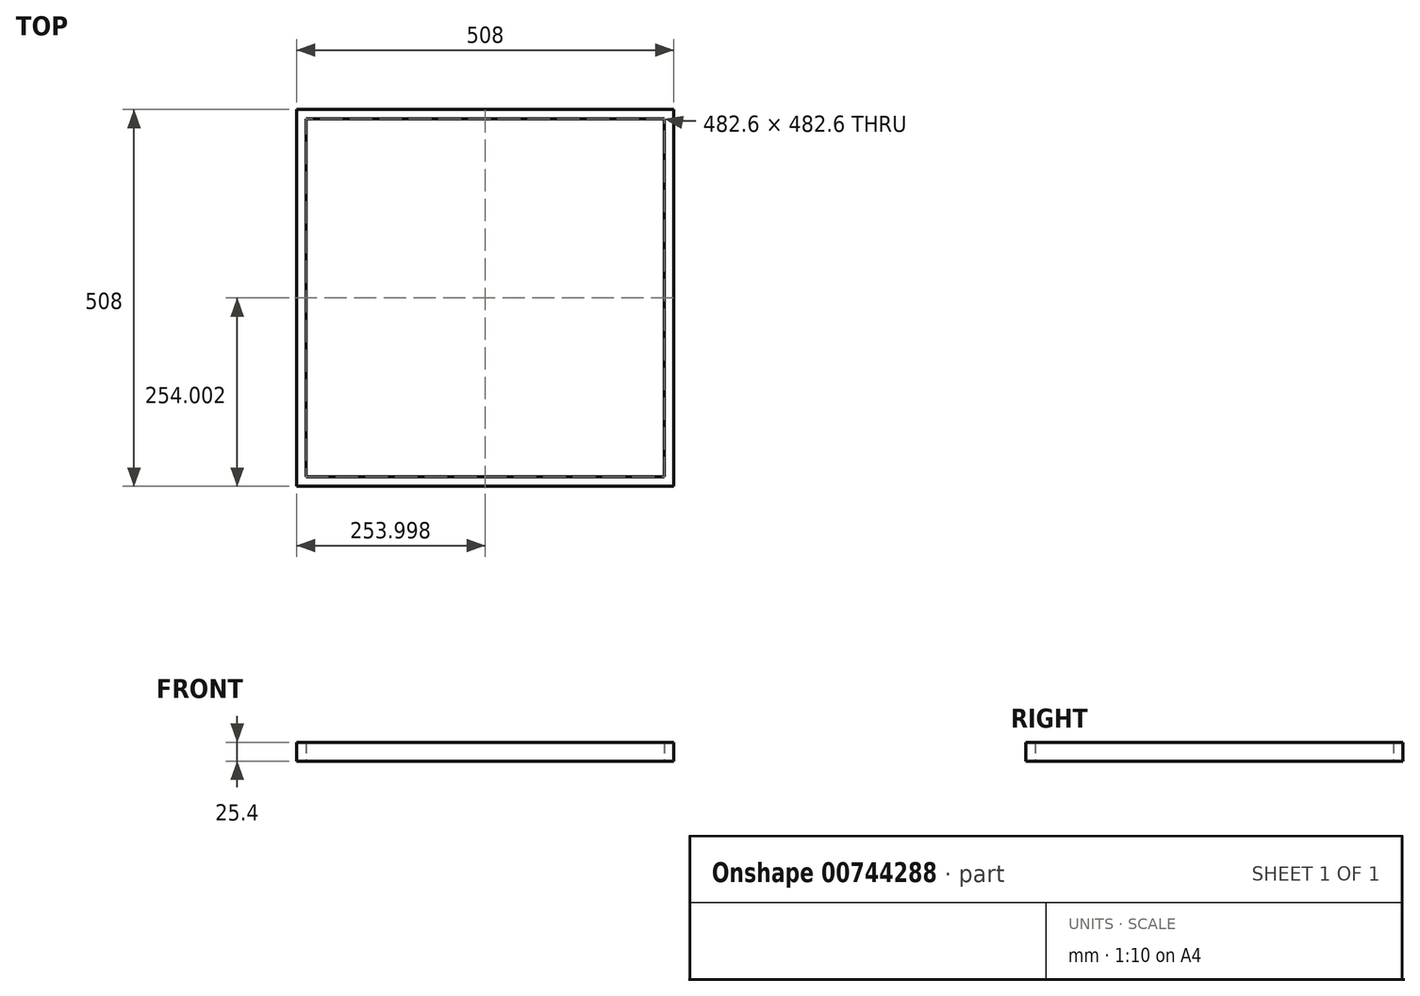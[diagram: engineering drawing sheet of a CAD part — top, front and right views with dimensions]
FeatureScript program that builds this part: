
annotation { "Feature Type Name" : "Feature", "Feature Type Description" : "" }
export const myFeature = defineFeature(function(context is Context, id is Id, definition is map)
    precondition{}
    {
        {
            var Q0;
            Q0=qCreatedBy(makeId("Top.planeOp"),FACE);
            var sketch = newSketch(context, id + "F0", { "sketchPlane" : qUnion([Q0])});
            skLineSegment(sketch, "E0.bottom", {"start": v(-73.52, 441.64) * mm, "end": v(434.48, 441.64) * mm});
            skLineSegment(sketch, "E0.top", {"start": v(-73.52, -66.36) * mm, "end": v(434.48, -66.36) * mm});
            skLineSegment(sketch, "E0.left", {"start": v(-73.52, 441.64) * mm, "end": v(-73.52, -66.36) * mm});
            skLineSegment(sketch, "E0.right", {"start": v(434.48, 441.64) * mm, "end": v(434.48, -66.36) * mm});
            skSolve(sketch);
        }
        {
            var Q0;
            Q0=makeQuery(id+"F0.imprint","IMPRINT",FACE,{"disambiguationData":[TD([[makeQuery(id+"F0.imprint","IMPRINT",EDGE,{"derivedFrom":sQuery(id+"F0.wireOp",EDGE,"E0.bottom")}),-1.0]])]});
            extrude(context, id + "F1", {"entities" : qUnion([Q0]), "depth" : 25.4 * mm, "offsetDistance" : 25.4 * mm});
        }
        {
            var Q0;
            Q0=makeQuery(id+"F1.opExtrude","CAP_FACE",FACE,{"disambiguationData":[OSD([sQuery(id+"F0.wireOp",EDGE,"E0.bottom"),sQuery(id+"F0.wireOp",EDGE,"E0.top"),sQuery(id+"F0.wireOp",EDGE,"E0.left"),sQuery(id+"F0.wireOp",EDGE,"E0.right")])],"isStart":false});
            shell(context, id + "F2", {"entities" : qUnion([Q0]), "thickness" : 12.7 * mm});
        }
        {
            var Q0;
            Q0=makeQuery(id+"F2.opShell","OFFSET_FACE",FACE,{"disambiguationData":[OSD([sQuery(id+"F0.wireOp",EDGE,"E0.bottom"),sQuery(id+"F0.wireOp",EDGE,"E0.top"),sQuery(id+"F0.wireOp",EDGE,"E0.left"),sQuery(id+"F0.wireOp",EDGE,"E0.right")])]});
            extrude(context, id + "F3", {"entities" : qUnion([Q0]), "operationType" : NewBodyOperationType.REMOVE, "oppositeDirection" : true, "depth" : 1396.1 * mm, "offsetDistance" : 25.4 * mm});
        }
    });
